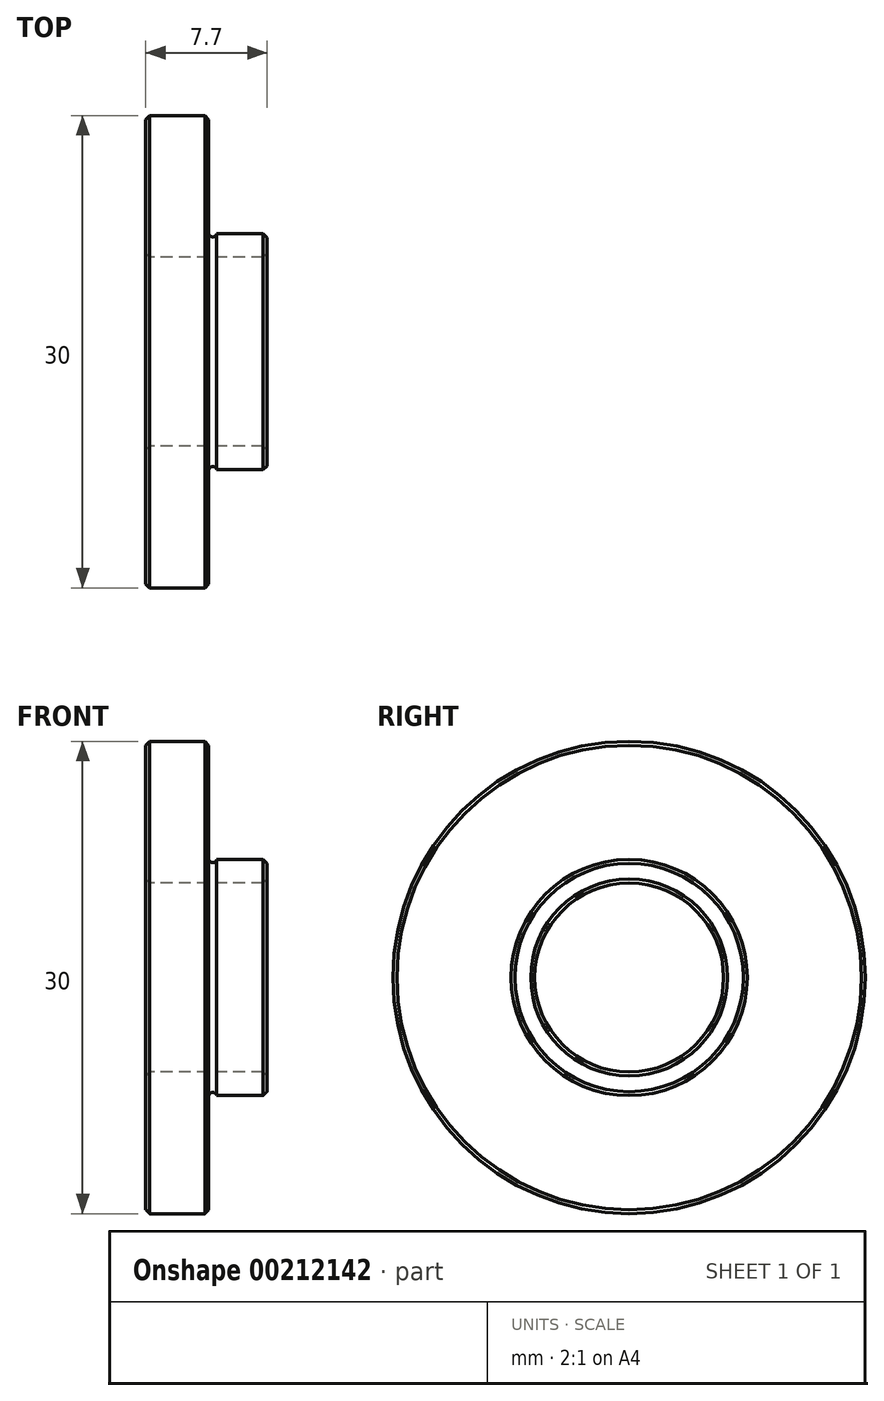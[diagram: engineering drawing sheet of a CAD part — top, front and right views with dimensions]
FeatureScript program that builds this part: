
annotation { "Feature Type Name" : "Feature", "Feature Type Description" : "" }
export const myFeature = defineFeature(function(context is Context, id is Id, definition is map)
    precondition{}
    {
        {
            var Q0;
            Q0=qCreatedBy(makeId("Right.planeOp"),FACE);
            var sketch = newSketch(context, id + "F0", { "sketchPlane" : qUnion([Q0])});
            skCircle(sketch, "E0", {"center": v(0, 0) * mm, "radius": 6 * mm});
            skCircle(sketch, "E1", {"center": v(0, 0) * mm, "radius": 7.5 * mm});
            skCircle(sketch, "E2", {"center": v(0, 0) * mm, "radius": 15 * mm});
            skSolve(sketch);
        }
        {
            var Q0;
            Q0=makeQuery(id+"F0.imprint","IMPRINT",FACE,{"disambiguationData":[TD([[makeQuery(id+"F0.imprint","IMPRINT",EDGE,{"derivedFrom":sQuery(id+"F0.wireOp",EDGE,"E1")}),-1.0]])]});
            extrude(context, id + "F1", {"entities" : qUnion([Q0]), "depth" : 4 * mm});
        }
        {
            var Q0;
            Q0=makeQuery(id+"F0.imprint","IMPRINT",FACE,{"disambiguationData":[TD([[makeQuery(id+"F0.imprint","IMPRINT",EDGE,{"derivedFrom":sQuery(id+"F0.wireOp",EDGE,"E0")}),-1.0]])]});
            extrude(context, id + "F2", {"entities" : qUnion([Q0]), "operationType" : NewBodyOperationType.ADD, "depth" : 7.7 * mm});
        }
        {
            var Q0;
            {var subQ0=sQuery(id+"F0.wireOp",EDGE,"E1");Q0=makeQuery(id+"F2.boolean.opBoolean","MERGE",FACE,{"derivedFrom":[makeQuery(id+"F1.opExtrude","CAP_FACE",FACE,{"disambiguationData":[OSD([subQ0,sQuery(id+"F0.wireOp",EDGE,"E2")])],"isStart":true}),makeQuery(id+"F2.opExtrude","CAP_FACE",FACE,{"disambiguationData":[OSD([sQuery(id+"F0.wireOp",EDGE,"E0"),subQ0])],"isStart":true})]});}
            var Q1;
            Q1=makeQuery(id+"F1.opExtrude","CAP_EDGE",EDGE,{"disambiguationData":[OSD([sQuery(id+"F0.wireOp",EDGE,"E2")])],"isStart":false});
            var Q2;
            Q2=makeQuery(id+"F2.opExtrude","CAP_EDGE",EDGE,{"disambiguationData":[OSD([sQuery(id+"F0.wireOp",EDGE,"E1")])],"isStart":false});
            var Q3;
            Q3=makeQuery(id+"F2.opExtrude","CAP_EDGE",EDGE,{"disambiguationData":[OSD([sQuery(id+"F0.wireOp",EDGE,"E0")])],"isStart":false});
            chamfer(context, id + "F3", {"entities" : qUnion([Q0, Q1, Q2, Q3]), "width" : .25 * mm, "tangentPropagation" : true});
        }
        {
            var Q0;
            Q0=qCreatedBy(makeId("Front.planeOp"),FACE);
            var sketch = newSketch(context, id + "F4", { "sketchPlane" : qUnion([Q0])});
            skLineSegment(sketch, "E3", {"start": v(0, 0) * mm, "end": v(4, 0) * mm, "construction": true});
            skLineSegment(sketch, "E4", {"start": v(4, 0) * mm, "end": v(4, 7.5) * mm, "construction": true});
            skLineSegment(sketch, "E5.0", {"start": v(4.25, 0) * mm, "end": v(4.25, 7.54) * mm, "construction": true});
            skLineSegment(sketch, "E6", {"start": v(4, 7.3) * mm, "end": v(4.25, 7.3) * mm, "construction": true});
            skLineSegment(sketch, "E7.0", {"start": v(4.5, 0) * mm, "end": v(4.5, 7.5) * mm, "construction": true});
            skArc(sketch, "E8", {"start": v(4, 7.5) * mm, "mid": v(4.25, 7.3) * mm, "end": v(4.5, 7.5) * mm});
            skLineSegment(sketch, "E9", {"start": v(4.5, 7.5) * mm, "end": v(4, 7.5) * mm});
            skSolve(sketch);
        }
        {
            var Q0;
            Q0=makeQuery(id+"F4.imprint","IMPRINT",FACE,{"disambiguationData":[TD([[makeQuery(id+"F4.imprint","IMPRINT",EDGE,{"derivedFrom":sQuery(id+"F4.wireOp",EDGE,"E8")}),1.0]])]});
            var Q1;
            Q1=sQuery(id+"F4.wireOp",EDGE,"E3");
            revolve(context, id + "F5", {"operationType" : NewBodyOperationType.REMOVE, "entities" : qUnion([Q0]), "axis" : qUnion([Q1]), "revolveType" : RevolveType.FULL, "oppositeDirection" : true});
        }
    });
